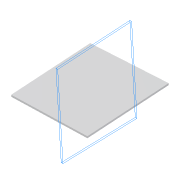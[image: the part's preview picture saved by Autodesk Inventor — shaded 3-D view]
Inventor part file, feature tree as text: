
AUTODESK INVENTOR PART (.ipt)
format: ipt  version: 2015 (Build 190159000, 159)  size: 89,088 bytes
history: native  units: mm
features: extrude x1, sketch x1, reference x1
ambient origin geometry x8: Origin, YZ Plane, XZ Plane, XY Plane, X Axis, Y Axis, Z Axis, Center Point
bodies: Solid1 (feature_tree)
feature tree (3):
  extrude  "Extrusion1"  Depth=5.0mm
  sketch  "Sketch1"  dims[d4=5.0mm d5=0.0mm d6=2.0mm]
  reference  "Reference6"
